# Revit family: Поли-Групп_ЗадвижкаШибернаяEAZ-ZT_DN1200
name_source: partatom
category: Арматура трубопроводов
units: mm (PartAtom-declared; Revit-internal decimal feet)

## family parameters
Всегда вертикально = Нет
На основе рабочей плоскости = Нет
Общий = Нет
При загрузке вырезать с полостями = Нет
Размер круглого соединителя = Использовать диаметр
Тип детали = Клапан - Вставляется

## types (1)
- DN1200 PN2
    ADSK_URL страницы изделия = https://www.polycorr.ru
    ADSK_Версия Revit = 2019
    ADSK_Единица измерения = шт
    ADSK_Завод-изготовитель = ООО ПК «Поли-Групп»
    ADSK_Марка = EAZ-KV-1 DN1200 PN2
    ADSK_Масса = 0
    ADSK_Масса_Текст = нет данных
    ADSK_Материал = Чугун GG25
    ADSK_Материал наименование = Высокопрочный чугун с шаровидным графитом (GGG-40)
    ADSK_Наименование = Задвижка шиберно-ножевая EAZ ZT DN1200 PN2 для воды и сточных вод межфланцевая
    ADSK_Наименование краткое = Задвижка шиберно-ножевая EAZ ZT DN1200 PN2
    D = 1455 мм
    D1 = 1380 мм
    D2 = 1328 мм
    DN = 1200 мм
    DO = 330 мм
    H = 2800 мм
    H1 = 3130 мм
    H2 = 1091 мм
    H3 = 728 мм
    Kv = 1.00 м³/ч
    L = 150 мм
    L1 = 90 мм
    O1 = 150 мм
    O2 = 528 мм
    PN = 2.0 бары
    d = 36 мм
    r = 10 мм
    Габаритные размеры = 150х1455х3857.5
    Класс герметичности = А по ГОСТ Р 9544-2015
    Коробка передач_Диаметр = 105 мм
    Крутящий момент = 0
    Материал Диска = Нержавеющая сталь марки 08Х18Н10
    Материал Ножа = Сталь нержавеющая
    Материал Рамы = Сталь синий
    Материал уплотнителя = NBR
    Назначение = Для установки в качестве запорного устройства на трубопроводах
    Нож_Выступ = 161 мм
    Нож_Толщина = 8 мм
    Подшипник_d = 40 мм
    Покрытие = Высококачественное эпоксидное покрытие толщиной 300 мкм
    Рабочая среда = Техническая вода, канализационные стоки, морская вода
    Разработчик = https://3dbim.pro
    Срок службы = 50 лет
    Стойка_t = 84 мм
    Стойка_Высота = 1609 мм
    Стойка_Длина = 150 мм
    Стойка_Толщина = 3 мм
    Ступор_Высота = 30 мм
    Ступор_Ширина = 30 мм
    ТВ = Поли-Групп_ЗадвижкаШибернаяEAZ-ZT_DN1200
    Температура рабочей среды = 0 до +70°С
    Тип привода = Штурвал
    Тип присоединения = Межфланцевое
    Шток_Диаметр = 30 мм
    Шток_Смещение = 38 мм
    Штурвал_Высота = 120 мм
